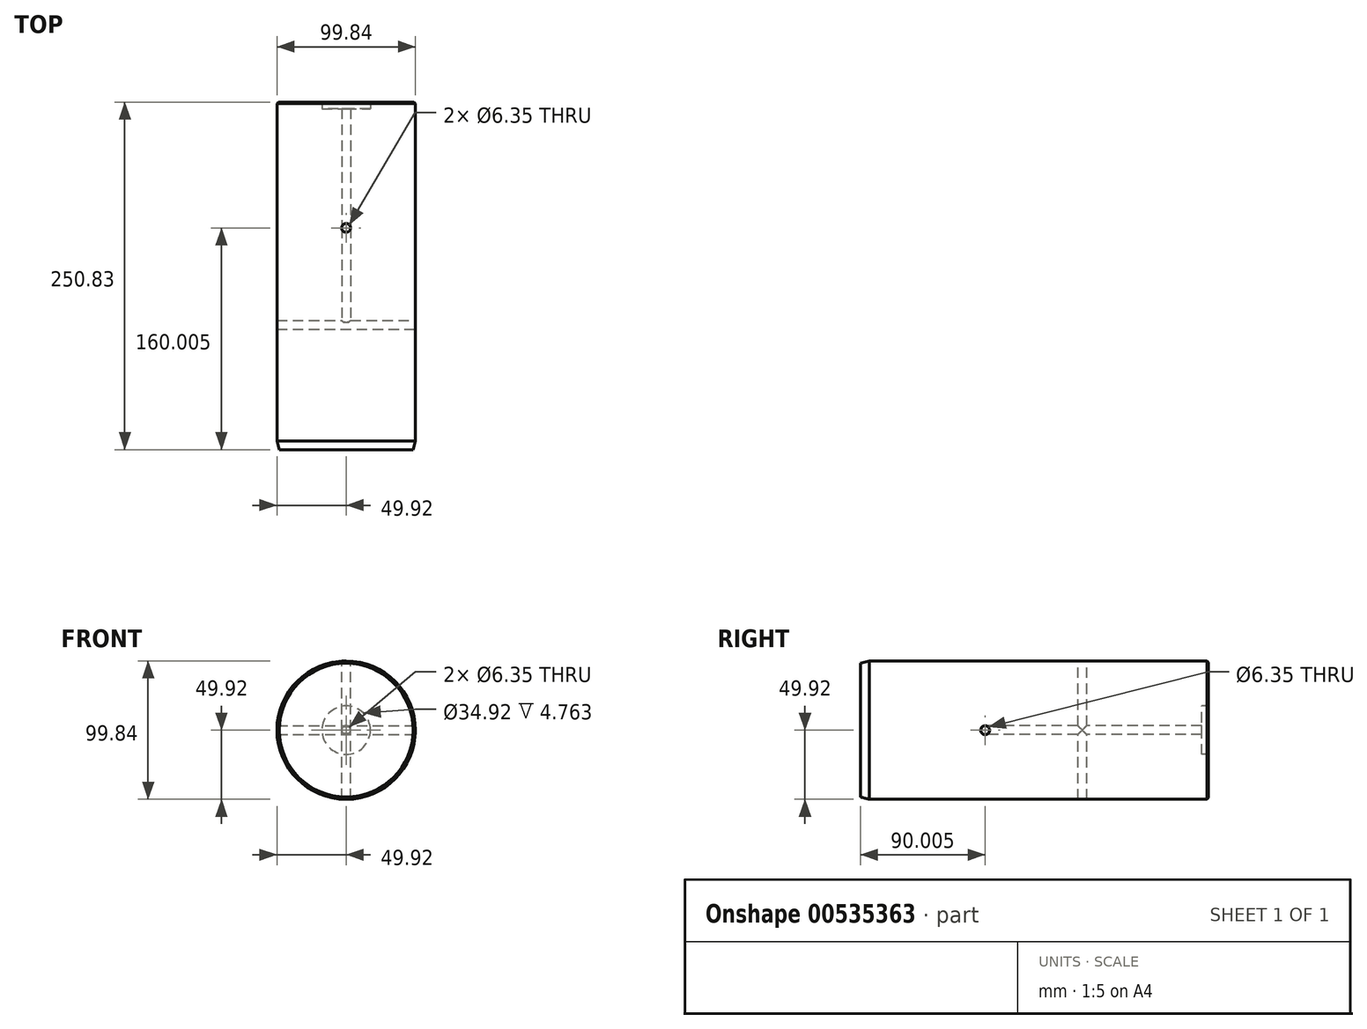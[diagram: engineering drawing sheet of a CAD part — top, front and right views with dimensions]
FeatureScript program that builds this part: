
annotation { "Feature Type Name" : "Feature", "Feature Type Description" : "" }
export const myFeature = defineFeature(function(context is Context, id is Id, definition is map)
    precondition{}
    {
        {
            var Q0;
            Q0=qCreatedBy(makeId("Front.planeOp"),FACE);
            var sketch = newSketch(context, id + "F0", { "sketchPlane" : qUnion([Q0])});
            skCircle(sketch, "E0", {"center": v(0, 0) * mm, "radius": 49.92 * mm});
            skSolve(sketch);
        }
        {
            var Q0;
            Q0=qSketchRegion(id+"F0",true);
            extrude(context, id + "F1", {"entities" : qUnion([Q0]), "depth" : 250.82 * mm, "offsetDistance" : 25.4 * mm});
        }
        {
            var Q0;
            Q0=makeQuery(id+"F1.opExtrude","CAP_EDGE",EDGE,{"disambiguationData":[OSD([sQuery(id+"F0.wireOp",EDGE,"E0")])],"isStart":false});
            chamfer(context, id + "F2", {"entities" : qUnion([Q0]), "chamferType" : ChamferType.OFFSET_ANGLE, "width" : 6.35 * mm, "oppositeDirection" : true, "angle" : 15 * degree, "tangentPropagation" : true});
        }
        {
            var Q0;
            Q0=qCreatedBy(makeId("Front.planeOp"),FACE);
            var sketch = newSketch(context, id + "F3", { "sketchPlane" : qUnion([Q0])});
            skPoint(sketch, "E1", {"position": v(0, 0) * mm});
            skSolve(sketch);
        }
        {
            var Q0;
            Q0=sQuery(id+"F3.wireOp",VERTEX,"E1");
            var Q1;
            Q1=makeQuery(id+"F1.opExtrude","SWEPT_BODY",BODY,{"disambiguationData":[OSD([sQuery(id+"F0.wireOp",EDGE,"E0")])]});
            hole(context, id + "F4", {"style" : HoleStyle.C_BORE, "endStyle" : HoleEndStyle.BLIND, "oppositeDirection" : true, "holeDiameter" : 6.35 * mm, "cBoreDiameter" : 34.92 * mm, "cBoreDepth" : 4.76 * mm, "holeDepth" : 158.75 * mm, "isTappedThrough" : true, "tappedDepth" : 12.7 * mm, "tapClearance" : 3, "startFromSketch" : true, "locations" : qUnion([Q0]), "scope" : qUnion([Q1])});
        }
        {
            var Q0;
            Q0=qCreatedBy(makeId("Right.planeOp"),FACE);
            var sketch = newSketch(context, id + "F5", { "sketchPlane" : qUnion([Q0])});
            skPoint(sketch, "E2", {"position": v(-160.83, 0) * mm});
            skCircle(sketch, "E3", {"center": v(-160.83, 0) * mm, "radius": 3.18 * mm});
            skSolve(sketch);
        }
        {
            var Q0;
            Q0 = qSketchRegion(id + "F5", true);
            extrude(context, id + "F6", {"entities" : qUnion([Q0]), "operationType" : NewBodyOperationType.REMOVE, "endBound" : BoundingType.THROUGH_ALL, "oppositeDirection" : true, "depth" : 25.4 * mm, "offsetDistance" : 25.4 * mm, "hasSecondDirection" : true, "secondDirectionBound" : BoundingType.THROUGH_ALL, "secondDirectionOppositeDirection" : false, "secondDirectionDepth" : 25.4 * mm});
        }
        {
            var Q0;
            Q0=qCreatedBy(makeId("Top.planeOp"),FACE);
            var sketch = newSketch(context, id + "F7", { "sketchPlane" : qUnion([Q0])});
            skCircle(sketch, "E4", {"center": v(0, -90.83) * mm, "radius": 3.18 * mm});
            skSolve(sketch);
        }
        {
            var Q0;
            Q0 = qSketchRegion(id + "F7", true);
            extrude(context, id + "F8", {"entities" : qUnion([Q0]), "operationType" : NewBodyOperationType.REMOVE, "endBound" : BoundingType.THROUGH_ALL, "oppositeDirection" : true, "depth" : 25.4 * mm, "offsetDistance" : 25.4 * mm, "hasSecondDirection" : true, "secondDirectionBound" : BoundingType.THROUGH_ALL, "secondDirectionOppositeDirection" : false, "secondDirectionDepth" : 25.4 * mm});
        }
        {
            var Q0;
            Q0=makeQuery(id+"F1.opExtrude","CAP_EDGE",EDGE,{"disambiguationData":[OSD([sQuery(id+"F0.wireOp",EDGE,"E0")])],"isStart":true});
            chamfer(context, id + "F9", {"entities" : qUnion([Q0]), "width" : 1 * mm, "tangentPropagation" : true});
        }
    });
